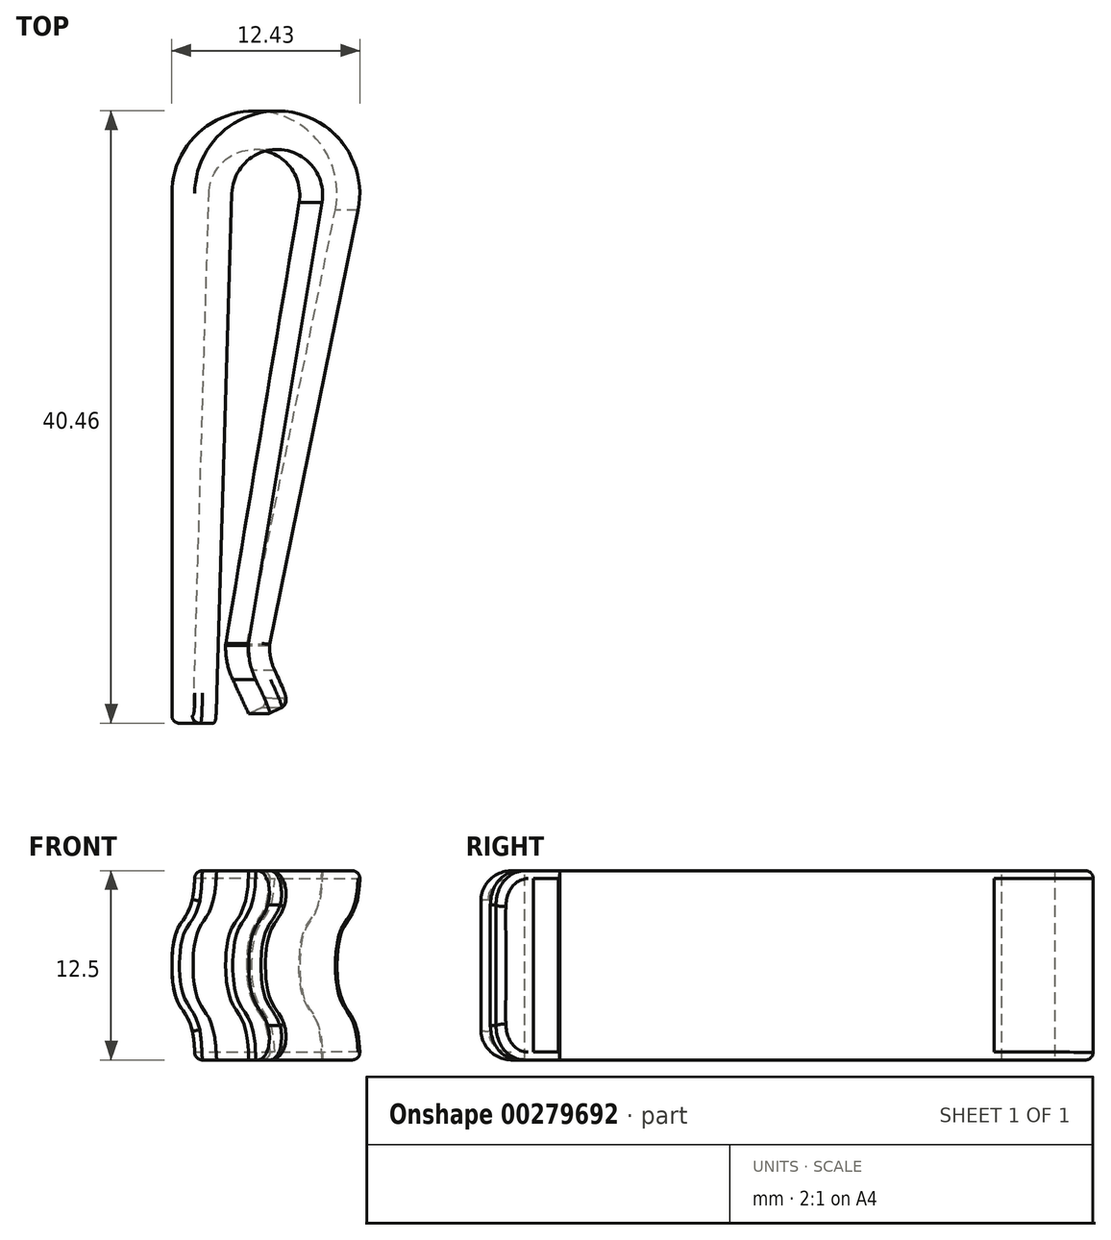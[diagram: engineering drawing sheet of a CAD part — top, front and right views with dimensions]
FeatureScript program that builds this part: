
annotation { "Feature Type Name" : "Feature", "Feature Type Description" : "" }
export const myFeature = defineFeature(function(context is Context, id is Id, definition is map)
    precondition{}
    {
        {
            var Q0;
            Q0=qCreatedBy(makeId("Top.planeOp"),FACE);
            var sketch = newSketch(context, id + "F0", { "sketchPlane" : qUnion([Q0])});
            skLineSegment(sketch, "E0", {"start": v(0, 0) * mm, "end": v(0, 35) * mm});
            skLineSegment(sketch, "E1", {"start": v(4.02, 2.89) * mm, "end": v(5.08, 0.62) * mm});
            skLineSegment(sketch, "E2", {"start": v(1.4, 0) * mm, "end": v(0, 0) * mm});
            skLineSegment(sketch, "E3", {"start": v(2.45, 35) * mm, "end": v(1.4, 0) * mm});
            skArc(sketch, "E4", {"start": v(0, 35) * mm, "mid": v(6, 40.43) * mm, "end": v(10.8, 33.91) * mm});
            skArc(sketch, "E5", {"start": v(2.45, 35) * mm, "mid": v(5.74, 37.9) * mm, "end": v(8.4, 34.42) * mm});
            skLineSegment(sketch, "E6", {"start": v(0, 35) * mm, "end": v(2.45, 35) * mm, "construction": true});
            skArc(sketch, "E7.filletArc", {"start": v(3.56, 5.15) * mm, "mid": v(3.66, 4) * mm, "end": v(4.02, 2.89) * mm});
            skLineSegment(sketch, "E8", {"start": v(5.08, 0.62) * mm, "end": v(6.35, 1.21) * mm});
            skLineSegment(sketch, "E9", {"start": v(6.35, 1.21) * mm, "end": v(5.3, 3.48) * mm});
            skArc(sketch, "E10", {"start": v(5.3, 3.48) * mm, "mid": v(5.03, 4.27) * mm, "end": v(4.95, 5.1) * mm});
            skLineSegment(sketch, "E11", {"start": v(4.96, 5.2) * mm, "end": v(4.95, 5.1) * mm});
            skLineSegment(sketch, "E12", {"start": v(3.56, 5.15) * mm, "end": v(3.56, 5.25) * mm});
            skLineSegment(sketch, "E13", {"start": v(8.4, 34.42) * mm, "end": v(3.56, 5.25) * mm});
            skLineSegment(sketch, "E14", {"start": v(10.8, 33.91) * mm, "end": v(4.96, 5.2) * mm});
            skLineSegment(sketch, "E15", {"start": v(8.4, 34.42) * mm, "end": v(10.8, 33.91) * mm, "construction": true});
            skLineSegment(sketch, "E16", {"start": v(4.96, 5.2) * mm, "end": v(3.56, 5.25) * mm, "construction": true});
            skSolve(sketch);
        }
        {
            var Q0;
            Q0=qCreatedBy(makeId("Front.planeOp"),FACE);
            var sketch = newSketch(context, id + "F1", { "sketchPlane" : qUnion([Q0])});
            skFitSpline(sketch, "E17", {"points": [v(0, 0) * mm, v(-1.2, 4) * mm, v(-1.2, 8.5) * mm, v(0, 12.5) * mm], "startDerivative": vector(0, 27.34) * mm, "endDerivative": vector(0, 27.34) * mm});
            skSolve(sketch);
        }
        {
            var Q0;
            Q0=qSketchRegion(id+"F0",true);
            var Q1;
            Q1=qConstructionFilter(qBodyType(qCreatedBy(id+"F0",EDGE),BodyType.WIRE),ConstructionObject.NO);
            var Q2;
            Q2=qConstructionFilter(qBodyType(qCreatedBy(id+"F1",EDGE),BodyType.WIRE),ConstructionObject.NO);
            sweep(context, id + "F2", {"profiles" : qUnion([Q0]), "surfaceProfiles" : qUnion([Q1]), "path" : qUnion([Q2]), "keepProfileOrientation" : true});
        }
        {
            var Q0;
            Q0=makeQuery(id+"F2.opSweep","CAP_EDGE",EDGE,{"disambiguationData":[OSD([sQuery(id+"F0.wireOp",EDGE,"E8"),sQuery(id+"F1.wireOp",VERTEX,"E17.end")])],"isStart":false});
            var Q1;
            Q1=makeQuery(id+"F2.opSweep","CAP_EDGE",EDGE,{"disambiguationData":[OSD([sQuery(id+"F0.wireOp",EDGE,"E8"),sQuery(id+"F1.wireOp",VERTEX,"E17.start")])],"isStart":true});
            var Q2;
            Q2=makeQuery(id+"F2.opSweep","CAP_EDGE",EDGE,{"disambiguationData":[OSD([sQuery(id+"F0.wireOp",EDGE,"E2"),sQuery(id+"F1.wireOp",VERTEX,"E17.end")])],"isStart":false});
            var Q3;
            Q3=makeQuery(id+"F2.opSweep","CAP_EDGE",EDGE,{"disambiguationData":[OSD([sQuery(id+"F0.wireOp",EDGE,"E2"),sQuery(id+"F1.wireOp",VERTEX,"E17.start")])],"isStart":true});
            fillet(context, id + "F3", {"entities" : qUnion([Q0, Q1, Q2, Q3]), "radius" : 2 * mm, "tangentPropagation" : true, "allowEdgeOverflow" : false});
        }
        {
            var Q0;
            Q0=makeQuery(id+"F3.opFillet","BLEND_EDGE",EDGE,{"blendedFrom":[makeQuery(id+"F2.opSweep","CAP_EDGE",EDGE,{"disambiguationData":[OSD([sQuery(id+"F0.wireOp",EDGE,"E8"),sQuery(id+"F1.wireOp",VERTEX,"E17.end")])],"isStart":false}),makeQuery(id+"F2.opSweep","SWEPT_FACE",FACE,{"disambiguationData":[OSD([sQuery(id+"F0.wireOp",EDGE,"E9"),sQuery(id+"F1.wireOp",EDGE,"E17")])]})],"blendedInto":[makeQuery(id+"F2.opSweep","SWEPT_FACE",FACE,{"disambiguationData":[OSD([sQuery(id+"F0.wireOp",EDGE,"E9"),sQuery(id+"F1.wireOp",EDGE,"E17")])]})]});
            var Q1;
            Q1=makeQuery(id+"F2.opSweep","CAP_EDGE",EDGE,{"disambiguationData":[OSD([sQuery(id+"F0.wireOp",EDGE,"E14"),sQuery(id+"F1.wireOp",VERTEX,"E17.end")])],"isStart":false});
            fillet(context, id + "F4", {"entities" : qUnion([Q0, Q1]), "radius" : 0.5 * mm, "tangentPropagation" : true, "allowEdgeOverflow" : false});
        }
    });
